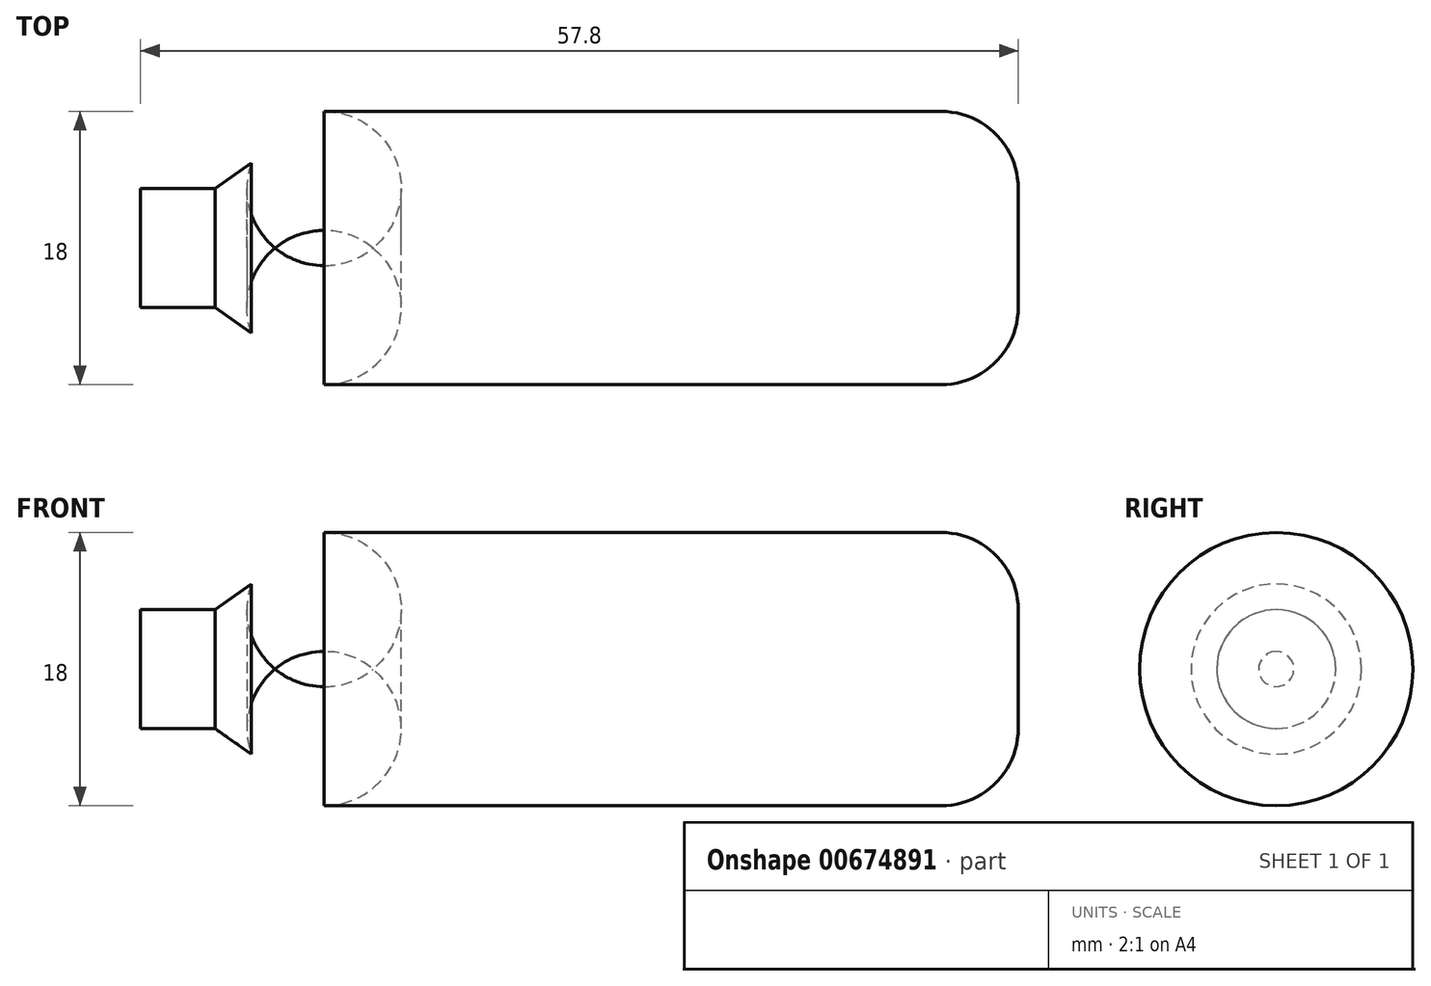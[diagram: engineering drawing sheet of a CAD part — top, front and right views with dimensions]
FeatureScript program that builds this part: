
annotation { "Feature Type Name" : "Feature", "Feature Type Description" : "" }
export const myFeature = defineFeature(function(context is Context, id is Id, definition is map)
    precondition{}
    {
        {
            var Q0;
            Q0=qCreatedBy(makeId("Right.planeOp"),FACE);
            var sketch = newSketch(context, id + "F0", { "sketchPlane" : qUnion([Q0])});
            skCircle(sketch, "E0", {"center": v(0, 0) * mm, "radius": 9 * mm});
            skSolve(sketch);
        }
        {
            var Q0;
            Q0=makeQuery(id+"F0.imprint","IMPRINT",FACE,{"disambiguationData":[TD([[makeQuery(id+"F0.imprint","IMPRINT",EDGE,{"derivedFrom":sQuery(id+"F0.wireOp",EDGE,"E0")}),1.0]])]});
            extrude(context, id + "F1", {"entities" : qUnion([Q0]), "depth" : 50.8 * mm, "offsetDistance" : 25.4 * mm});
        }
        {
            var Q0;
            Q0=makeQuery(id+"F1.opExtrude","CAP_FACE",FACE,{"disambiguationData":[OSD([sQuery(id+"F0.wireOp",EDGE,"E0")])],"isStart":false});
            var Q1;
            Q1=makeQuery(id+"F1.opExtrude","CAP_EDGE",EDGE,{"disambiguationData":[OSD([sQuery(id+"F0.wireOp",EDGE,"E0")])],"isStart":true});
            fillet(context, id + "F2", {"entities" : qUnion([Q0, Q1]), "radius" : 5.08 * mm, "tangentPropagation" : true, "allowEdgeOverflow" : false});
        }
        {
            var Q0;
            Q0=makeQuery(id+"F1.opExtrude","CAP_FACE",FACE,{"disambiguationData":[OSD([sQuery(id+"F0.wireOp",EDGE,"E0")])],"isStart":true});
            extrude(context, id + "F3", {"entities" : qUnion([Q0]), "operationType" : NewBodyOperationType.ADD, "depth" : 7 * mm, "offsetDistance" : 25.4 * mm});
        }
        {
            var Q0;
            {var subQ0=sQuery(id+"F0.wireOp",EDGE,"E0");Q0=makeQuery(id+"F3.boolean.opBoolean","MERGE",EDGE,{"derivedFrom":[makeQuery(id+"F2.opFillet","BLEND_EDGE",EDGE,{"blendedFrom":[makeQuery(id+"F1.opExtrude","CAP_EDGE",EDGE,{"disambiguationData":[OSD([subQ0])],"isStart":true}),makeQuery(id+"F1.opExtrude","CAP_FACE",FACE,{"disambiguationData":[OSD([subQ0])],"isStart":true})],"blendedInto":[makeQuery(id+"F1.opExtrude","CAP_FACE",FACE,{"disambiguationData":[OSD([subQ0])],"isStart":true})]}),makeQuery(id+"F3.opExtrude","CAP_EDGE",EDGE,{"disambiguationData":[OSD([subQ0])],"isStart":true})]});}
            chamfer(context, id + "F4", {"entities" : qUnion([Q0]), "width" : 2.54 * mm, "tangentPropagation" : true});
        }
    });
